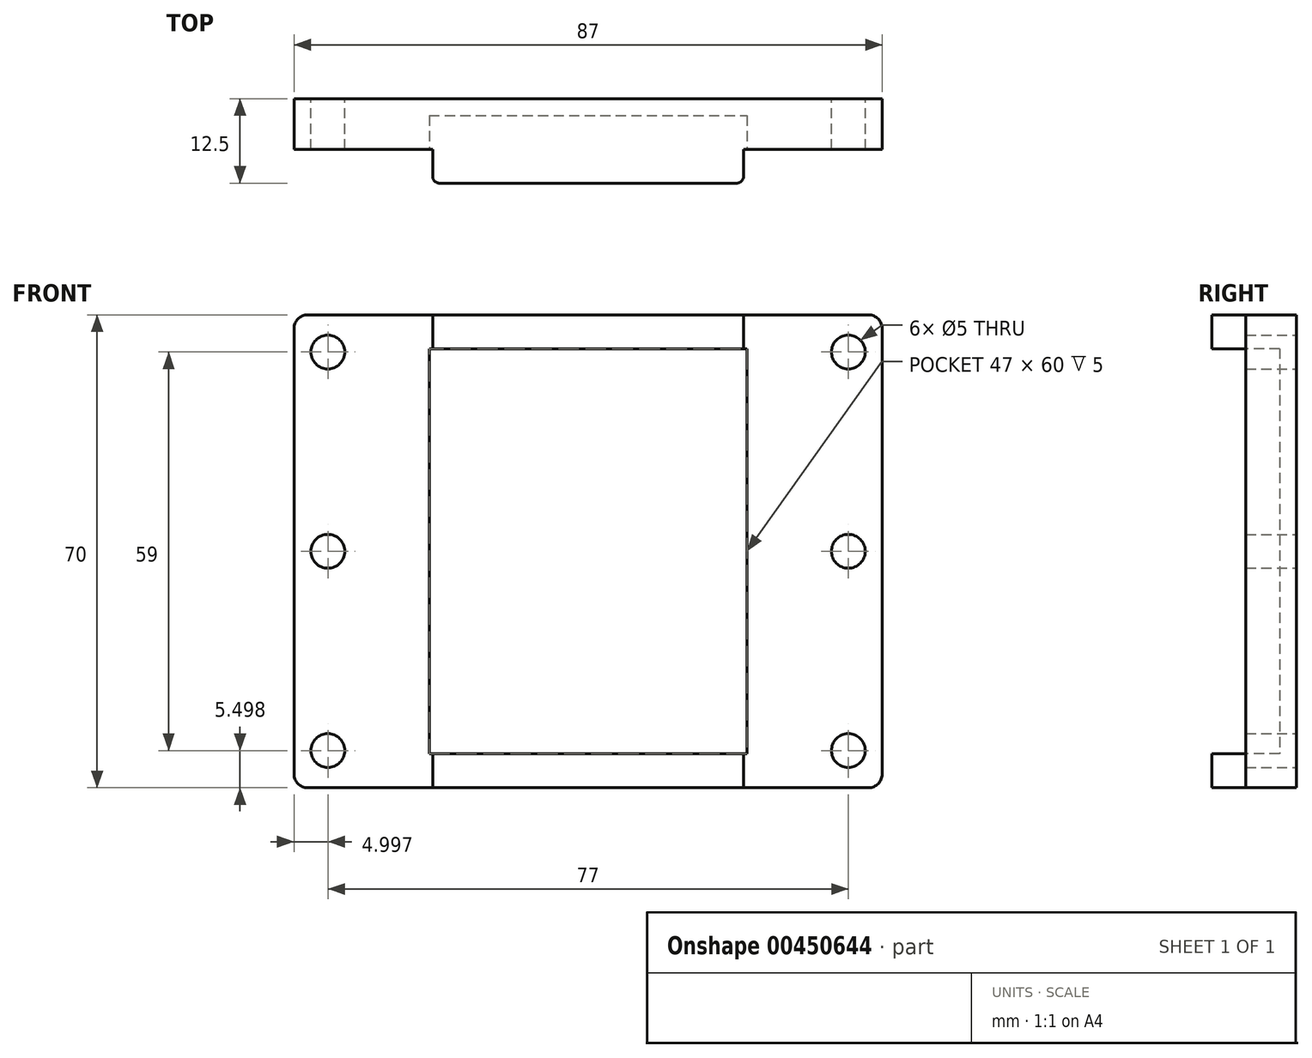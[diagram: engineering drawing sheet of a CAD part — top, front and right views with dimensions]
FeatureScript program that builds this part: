
annotation { "Feature Type Name" : "Feature", "Feature Type Description" : "" }
export const myFeature = defineFeature(function(context is Context, id is Id, definition is map)
    precondition{}
    {
        {
            var Q0;
            Q0=qCreatedBy(makeId("Front.planeOp"),FACE);
            var sketch = newSketch(context, id + "F0", { "sketchPlane" : qUnion([Q0])});
            skLineSegment(sketch, "E0.bottom", {"start": v(-99.48, 55.35) * mm, "end": v(-12.48, 55.35) * mm});
            skLineSegment(sketch, "E0.top", {"start": v(-99.48, -14.65) * mm, "end": v(-12.48, -14.65) * mm});
            skLineSegment(sketch, "E0.left", {"start": v(-99.48, 55.35) * mm, "end": v(-99.48, -14.65) * mm});
            skLineSegment(sketch, "E0.right", {"start": v(-12.48, 55.35) * mm, "end": v(-12.48, -14.65) * mm});
            skCircle(sketch, "E1", {"center": v(-94.48, -9.15) * mm, "radius": 2.5 * mm});
            skCircle(sketch, "E2.0.1.0", {"center": v(-94.48, 20.35) * mm, "radius": 2.5 * mm});
            skCircle(sketch, "E2.0.2.0", {"center": v(-94.48, 49.85) * mm, "radius": 2.5 * mm});
            skCircle(sketch, "E2.1.0.0", {"center": v(-17.48, -9.15) * mm, "radius": 2.5 * mm});
            skCircle(sketch, "E2.1.1.0", {"center": v(-17.48, 20.35) * mm, "radius": 2.5 * mm});
            skCircle(sketch, "E2.1.2.0", {"center": v(-17.48, 49.85) * mm, "radius": 2.5 * mm});
            skLineSegment(sketch, "E2.direction1", {"start": v(-94.48, -9.15) * mm, "end": v(-17.48, -9.15) * mm, "construction": true});
            skLineSegment(sketch, "E2.direction2", {"start": v(-94.48, -9.15) * mm, "end": v(-94.48, 20.35) * mm, "construction": true});
            skSolve(sketch);
        }
        {
            var Q0;
            Q0=makeQuery(id+"F0.imprint","IMPRINT",FACE,{"disambiguationData":[TD([[makeQuery(id+"F0.imprint","IMPRINT",EDGE,{"derivedFrom":sQuery(id+"F0.wireOp",EDGE,"E0.bottom")}),-1.0]])]});
            extrude(context, id + "F1", {"entities" : qUnion([Q0]), "depth" : 7.5 * mm});
        }
        {
            var Q0;
            Q0=makeQuery(id+"F1.opExtrude","CAP_FACE",FACE,{"disambiguationData":[OSD([sQuery(id+"F0.wireOp",EDGE,"E0.bottom"),sQuery(id+"F0.wireOp",EDGE,"E0.top"),sQuery(id+"F0.wireOp",EDGE,"E0.left"),sQuery(id+"F0.wireOp",EDGE,"E0.right"),sQuery(id+"F0.wireOp",EDGE,"E1"),sQuery(id+"F0.wireOp",EDGE,"E2.0.1.0"),sQuery(id+"F0.wireOp",EDGE,"E2.0.2.0"),sQuery(id+"F0.wireOp",EDGE,"E2.1.0.0"),sQuery(id+"F0.wireOp",EDGE,"E2.1.1.0"),sQuery(id+"F0.wireOp",EDGE,"E2.1.2.0")])],"isStart":false});
            var sketch = newSketch(context, id + "F2", { "sketchPlane" : qUnion([Q0])});
            skLineSegment(sketch, "E3.bottom", {"start": v(-79.48, 50.35) * mm, "end": v(-32.48, 50.35) * mm});
            skLineSegment(sketch, "E3.top", {"start": v(-79.48, -9.65) * mm, "end": v(-32.48, -9.65) * mm});
            skLineSegment(sketch, "E3.left", {"start": v(-79.48, 50.35) * mm, "end": v(-79.48, -9.65) * mm});
            skLineSegment(sketch, "E3.right", {"start": v(-32.48, 50.35) * mm, "end": v(-32.48, -9.65) * mm});
            skSolve(sketch);
        }
        {
            var Q0;
            Q0=makeQuery(id+"F2.imprint","IMPRINT",FACE,{"disambiguationData":[TD([[makeQuery(id+"F2.imprint","IMPRINT",EDGE,{"derivedFrom":sQuery(id+"F2.wireOp",EDGE,"E3.bottom")}),-1.0]])]});
            extrude(context, id + "F3", {"entities" : qUnion([Q0]), "operationType" : NewBodyOperationType.REMOVE, "oppositeDirection" : true, "depth" : 5 * mm});
        }
        {
            var Q0;
            Q0=makeQuery(id+"F1.opExtrude","CAP_FACE",FACE,{"disambiguationData":[OSD([sQuery(id+"F0.wireOp",EDGE,"E0.bottom"),sQuery(id+"F0.wireOp",EDGE,"E0.top"),sQuery(id+"F0.wireOp",EDGE,"E0.left"),sQuery(id+"F0.wireOp",EDGE,"E0.right"),sQuery(id+"F0.wireOp",EDGE,"E1"),sQuery(id+"F0.wireOp",EDGE,"E2.0.1.0"),sQuery(id+"F0.wireOp",EDGE,"E2.0.2.0"),sQuery(id+"F0.wireOp",EDGE,"E2.1.0.0"),sQuery(id+"F0.wireOp",EDGE,"E2.1.1.0"),sQuery(id+"F0.wireOp",EDGE,"E2.1.2.0")])],"isStart":false});
            var sketch = newSketch(context, id + "F4", { "sketchPlane" : qUnion([Q0])});
            skLineSegment(sketch, "E4.bottom", {"start": v(-78.98, 50.35) * mm, "end": v(-32.98, 50.35) * mm});
            skLineSegment(sketch, "E4.top", {"start": v(-78.98, 55.35) * mm, "end": v(-32.98, 55.35) * mm});
            skLineSegment(sketch, "E4.left", {"start": v(-78.98, 50.35) * mm, "end": v(-78.98, 55.35) * mm});
            skLineSegment(sketch, "E4.right", {"start": v(-32.98, 50.35) * mm, "end": v(-32.98, 55.35) * mm});
            skLineSegment(sketch, "E5.bottom", {"start": v(-32.98, -9.65) * mm, "end": v(-78.98, -9.65) * mm});
            skLineSegment(sketch, "E5.top", {"start": v(-32.98, -14.65) * mm, "end": v(-78.98, -14.65) * mm});
            skLineSegment(sketch, "E5.left", {"start": v(-32.98, -9.65) * mm, "end": v(-32.98, -14.65) * mm});
            skLineSegment(sketch, "E5.right", {"start": v(-78.98, -9.65) * mm, "end": v(-78.98, -14.65) * mm});
            skSolve(sketch);
        }
        {
            var Q0;
            Q0=makeQuery(id+"F4.imprint","IMPRINT",FACE,{"disambiguationData":[TD([[makeQuery(id+"F4.imprint","IMPRINT",EDGE,{"derivedFrom":sQuery(id+"F4.wireOp",EDGE,"E4.bottom")}),1.0]])]});
            var Q1;
            Q1=makeQuery(id+"F4.imprint","IMPRINT",FACE,{"disambiguationData":[TD([[makeQuery(id+"F4.imprint","IMPRINT",EDGE,{"derivedFrom":sQuery(id+"F4.wireOp",EDGE,"E5.bottom")}),-1.0]])]});
            extrude(context, id + "F5", {"entities" : qUnion([Q0, Q1]), "operationType" : NewBodyOperationType.ADD, "depth" : 5 * mm});
        }
        {
            var Q0;
            Q0=makeQuery(id+"F5.opExtrude","CAP_EDGE",EDGE,{"disambiguationData":[OSD([sQuery(id+"F4.wireOp",EDGE,"E4.left")])],"isStart":false});
            var Q1;
            Q1=makeQuery(id+"F5.opExtrude","CAP_EDGE",EDGE,{"disambiguationData":[OSD([sQuery(id+"F4.wireOp",EDGE,"E4.right")])],"isStart":false});
            var Q2;
            Q2=makeQuery(id+"F5.opExtrude","CAP_EDGE",EDGE,{"disambiguationData":[OSD([sQuery(id+"F4.wireOp",EDGE,"E5.left")])],"isStart":false});
            var Q3;
            Q3=makeQuery(id+"F5.opExtrude","CAP_EDGE",EDGE,{"disambiguationData":[OSD([sQuery(id+"F4.wireOp",EDGE,"E5.right")])],"isStart":false});
            fillet(context, id + "F6", {"entities" : qUnion([Q0, Q1, Q2, Q3]), "radius" : 1 * mm, "tangentPropagation" : true, "allowEdgeOverflow" : false});
        }
        {
            var Q0;
            Q0=makeQuery(id+"F1.opExtrude","SWEPT_EDGE",EDGE,{"disambiguationData":[OSD([sQuery(id+"F0.wireOp",EDGE,"E0.top"),sQuery(id+"F0.wireOp",EDGE,"E0.left")])]});
            var Q1;
            Q1=makeQuery(id+"F1.opExtrude","SWEPT_EDGE",EDGE,{"disambiguationData":[OSD([sQuery(id+"F0.wireOp",EDGE,"E0.top"),sQuery(id+"F0.wireOp",EDGE,"E0.right")])]});
            var Q2;
            Q2=makeQuery(id+"F1.opExtrude","SWEPT_EDGE",EDGE,{"disambiguationData":[OSD([sQuery(id+"F0.wireOp",EDGE,"E0.bottom"),sQuery(id+"F0.wireOp",EDGE,"E0.right")])]});
            var Q3;
            Q3=makeQuery(id+"F1.opExtrude","SWEPT_EDGE",EDGE,{"disambiguationData":[OSD([sQuery(id+"F0.wireOp",EDGE,"E0.bottom"),sQuery(id+"F0.wireOp",EDGE,"E0.left")])]});
            fillet(context, id + "F7", {"entities" : qUnion([Q0, Q1, Q2, Q3]), "radius" : 2 * mm, "tangentPropagation" : true, "allowEdgeOverflow" : false});
        }
    });
